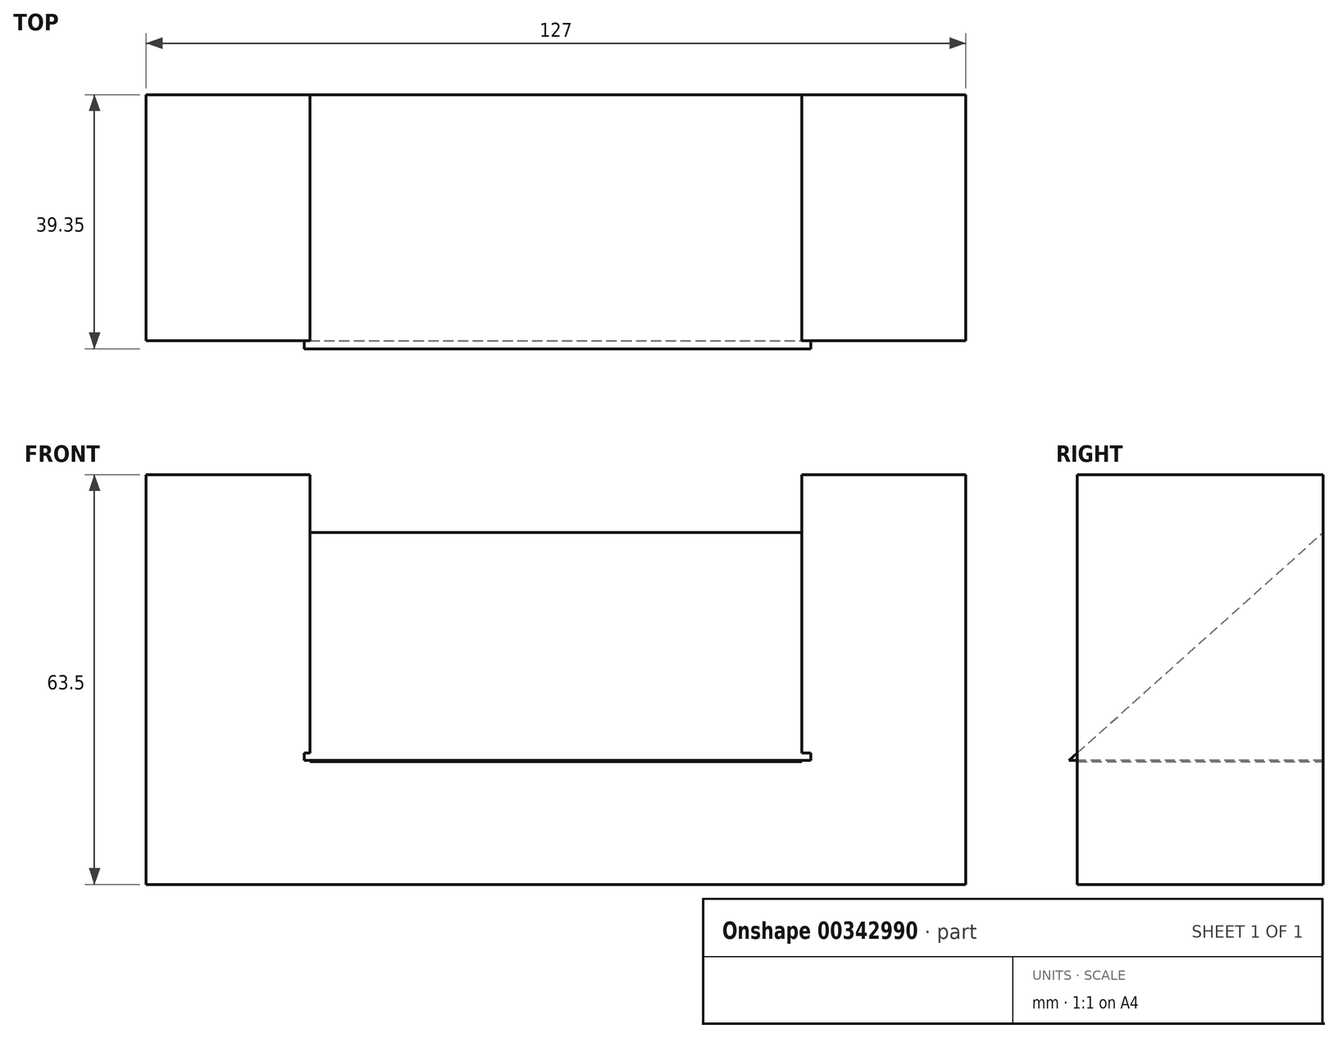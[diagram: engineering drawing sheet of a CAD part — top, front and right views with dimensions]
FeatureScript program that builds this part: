
annotation { "Feature Type Name" : "Feature", "Feature Type Description" : "" }
export const myFeature = defineFeature(function(context is Context, id is Id, definition is map)
    precondition{}
    {
        {
            var Q0;
            Q0=qCreatedBy(makeId("Front.planeOp"),FACE);
            var sketch = newSketch(context, id + "F0", { "sketchPlane" : qUnion([Q0])});
            skLineSegment(sketch, "E0", {"start": v(-67.43, -36) * mm, "end": v(59.57, -36) * mm});
            skLineSegment(sketch, "E1", {"start": v(59.57, -36) * mm, "end": v(59.57, 27.5) * mm});
            skLineSegment(sketch, "E2", {"start": v(59.57, 27.5) * mm, "end": v(34.17, 27.5) * mm});
            skLineSegment(sketch, "E3", {"start": v(34.17, 27.5) * mm, "end": v(34.17, -16.95) * mm});
            skLineSegment(sketch, "E4", {"start": v(-67.43, -36) * mm, "end": v(-67.43, 27.5) * mm});
            skLineSegment(sketch, "E5", {"start": v(-67.43, 27.5) * mm, "end": v(-42.03, 27.5) * mm});
            skLineSegment(sketch, "E6", {"start": v(-42.03, 27.5) * mm, "end": v(-42.03, -16.95) * mm});
            skLineSegment(sketch, "E7", {"start": v(-42.03, -16.95) * mm, "end": v(34.17, -16.95) * mm});
            skSolve(sketch);
        }
        {
            var Q0;
            Q0=makeQuery(id+"F0.imprint","IMPRINT",FACE,{"disambiguationData":[TD([[makeQuery(id+"F0.imprint","IMPRINT",EDGE,{"derivedFrom":sQuery(id+"F0.wireOp",EDGE,"E0")}),1.0]])]});
            extrude(context, id + "F1", {"entities" : qUnion([Q0]), "depth" : 38.1 * mm});
        }
        {
            var Q0;
            Q0=qCreatedBy(makeId("Right.planeOp"),FACE);
            var sketch = newSketch(context, id + "F2", { "sketchPlane" : qUnion([Q0])});
            skLineSegment(sketch, "E8", {"start": v(-39.35, -16.76) * mm, "end": v(0, -16.76) * mm});
            skLineSegment(sketch, "E9", {"start": v(0, -16.76) * mm, "end": v(0, 18.5) * mm});
            skLineSegment(sketch, "E10", {"start": v(0, 18.5) * mm, "end": v(-39.35, -16.76) * mm});
            skSolve(sketch);
        }
        {
            var Q0;
            Q0 = qSketchRegion(id + "F2", true);
            extrude(context, id + "F3", {"entities" : qUnion([Q0]), "operationType" : NewBodyOperationType.ADD, "depth" : 35.56 * mm, "hasSecondDirection" : true, "secondDirectionOppositeDirection" : true, "secondDirectionDepth" : 42.93 * mm});
        }
    });
